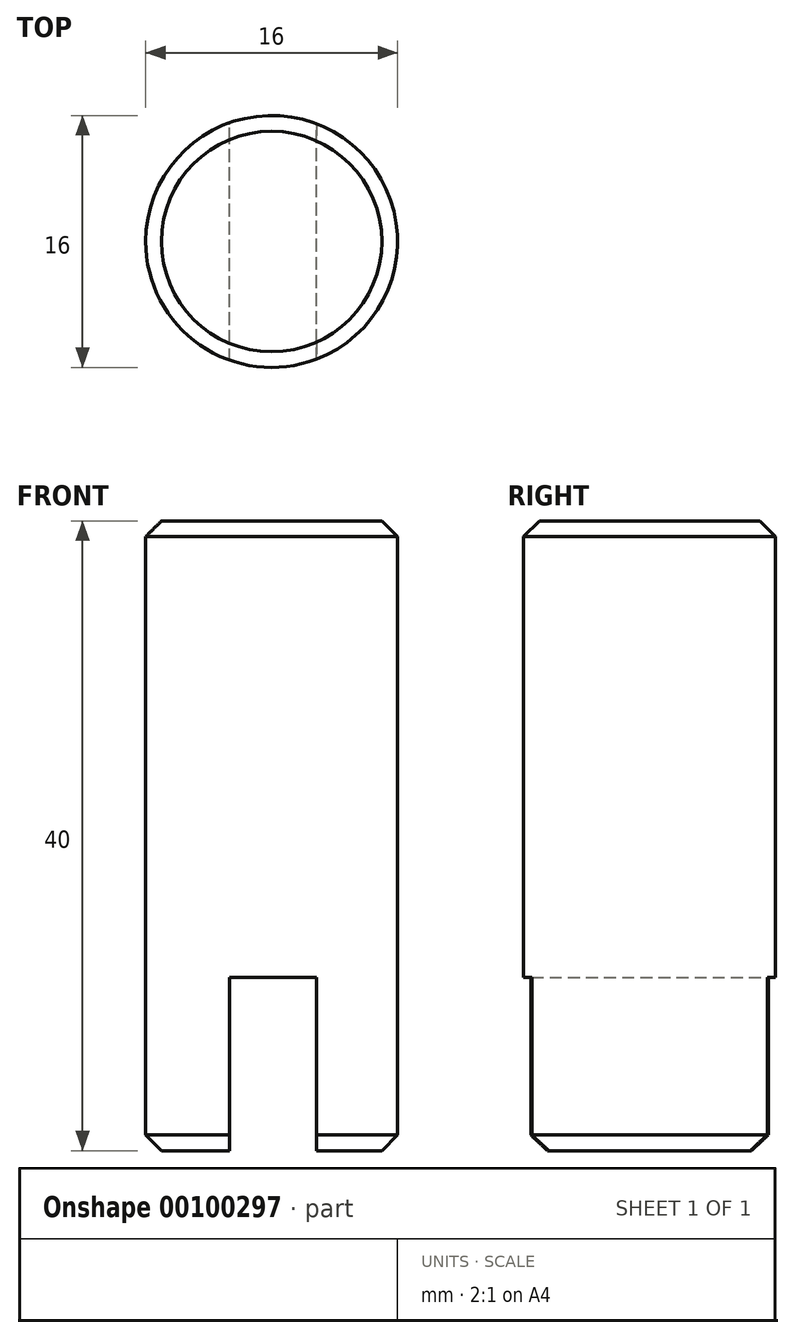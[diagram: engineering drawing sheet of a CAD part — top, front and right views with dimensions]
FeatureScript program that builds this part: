
annotation { "Feature Type Name" : "Feature", "Feature Type Description" : "" }
export const myFeature = defineFeature(function(context is Context, id is Id, definition is map)
    precondition{}
    {
        {
            var Q0;
            Q0=qCreatedBy(makeId("Front.planeOp"),FACE);
            var sketch = newSketch(context, id + "F0", { "sketchPlane" : qUnion([Q0])});
            skLineSegment(sketch, "E0.bottom", {"start": v(-8, 40) * mm, "end": v(0, 40) * mm});
            skLineSegment(sketch, "E0.top", {"start": v(-8, 0) * mm, "end": v(0, 0) * mm});
            skLineSegment(sketch, "E0.left", {"start": v(-8, 40) * mm, "end": v(-8, 0) * mm});
            skLineSegment(sketch, "E0.right", {"start": v(0, 40) * mm, "end": v(0, 0) * mm});
            skSolve(sketch);
        }
        {
            var Q0;
            Q0=makeQuery(id+"F0.imprint","IMPRINT",FACE,{"disambiguationData":[TD([[makeQuery(id+"F0.imprint","IMPRINT",EDGE,{"derivedFrom":sQuery(id+"F0.wireOp",EDGE,"E0.bottom")}),-1.0]])]});
            var Q1;
            Q1=sQuery(id+"F0.wireOp",EDGE,"E0.right");
            revolve(context, id + "F1", {"entities" : qUnion([Q0]), "axis" : qUnion([Q1]), "revolveType" : RevolveType.FULL});
        }
        {
            var Q0;
            Q0=qCreatedBy(makeId("Front.planeOp"),FACE);
            var sketch = newSketch(context, id + "F2", { "sketchPlane" : qUnion([Q0])});
            skLineSegment(sketch, "E1.bottom", {"start": v(-2.66, 11) * mm, "end": v(2.84, 11) * mm});
            skLineSegment(sketch, "E1.top", {"start": v(-2.66, 0) * mm, "end": v(2.84, 0) * mm});
            skLineSegment(sketch, "E1.left", {"start": v(-2.66, 11) * mm, "end": v(-2.66, 0) * mm});
            skLineSegment(sketch, "E1.right", {"start": v(2.84, 11) * mm, "end": v(2.84, 0) * mm});
            skSolve(sketch);
        }
        {
            var Q0;
            Q0=qSketchRegion(id+"F2",true);
            extrude(context, id + "F3", {"entities" : qUnion([Q0]), "operationType" : NewBodyOperationType.REMOVE, "endBound" : BoundingType.SYMMETRIC, "depth" : 25 * mm});
        }
        {
            var Q0;
            Q0=makeQuery(id+"F1.opRevolve","SWEPT_EDGE",EDGE,{"disambiguationData":[OSD([sQuery(id+"F0.wireOp",EDGE,"E0.bottom"),sQuery(id+"F0.wireOp",EDGE,"E0.left")])]});
            var Q1;
            {var subQ0=sQuery(id+"F0.wireOp",EDGE,"E0.top");var subQ1=sQuery(id+"F0.wireOp",EDGE,"E0.left");Q1=makeQuery(id+"F3.boolean.opBoolean","SPLIT",EDGE,{"disambiguationData":[TD([makeQuery(id+"F3.opExtrude","SWEPT_FACE",FACE,{"disambiguationData":[OSD([sQuery(id+"F2.wireOp",EDGE,"E1.right")])]})])],"derivedFrom":makeQuery(id+"F1.opRevolve","SWEPT_EDGE",EDGE,{"disambiguationData":[OSD([subQ0,subQ1])]})});}
            var Q2;
            {var subQ0=sQuery(id+"F0.wireOp",EDGE,"E0.top");var subQ1=sQuery(id+"F0.wireOp",EDGE,"E0.left");Q2=makeQuery(id+"F3.boolean.opBoolean","SPLIT",EDGE,{"disambiguationData":[TD([makeQuery(id+"F3.opExtrude","SWEPT_FACE",FACE,{"disambiguationData":[OSD([sQuery(id+"F2.wireOp",EDGE,"E1.left")])]})])],"derivedFrom":makeQuery(id+"F1.opRevolve","SWEPT_EDGE",EDGE,{"disambiguationData":[OSD([subQ0,subQ1])]})});}
            chamfer(context, id + "F4", {"entities" : qUnion([Q0, Q1, Q2]), "width" : 1 * mm, "tangentPropagation" : true});
        }
    });
